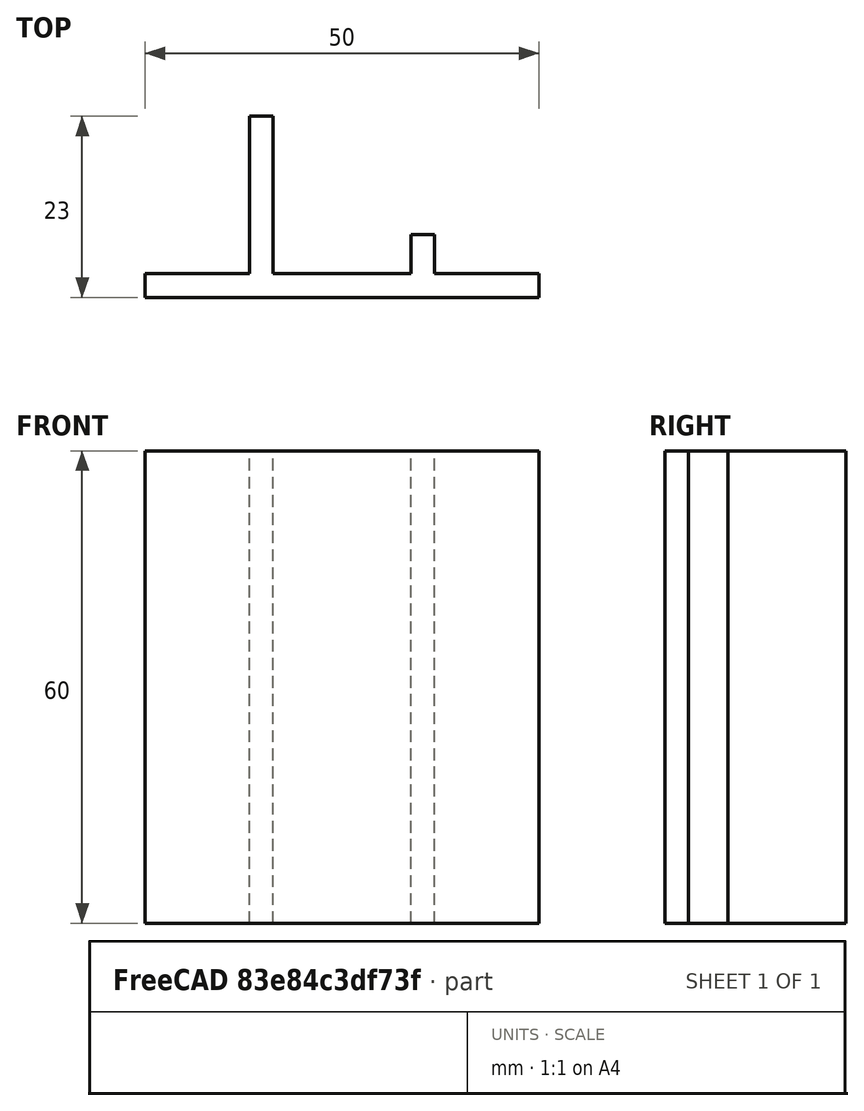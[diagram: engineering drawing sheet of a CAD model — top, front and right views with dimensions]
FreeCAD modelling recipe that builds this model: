
FCSTD DOCUMENT  (FreeCAD 0.20R29603 (Git))
Label: 3d_stand
License: All rights reserved
LicenseURL: http://en.wikipedia.org/wiki/All_rights_reserved
objects: Sketcher::SketchObject×1, PartDesign::Pad×1, PartDesign::Body×1
note: 4 computed .brp shape members not serialized (recipe doc carries the construction recipe); baked Part::Feature solids carry a one-line shape summary decoded from their .brp

FEATURE [Sketcher::SketchObject] Sketch
  FullyConstrained = true
  MapMode = 5
  Support = -> [XY_Plane]
  sketch-geometry (12):
    g0: LineSegment StartX=-24.88 StartY=-4.7 StartZ=0 EndX=25.12 EndY=-4.7 EndZ=0
    g1: LineSegment StartX=25.12 StartY=-4.7 StartZ=0 EndX=25.12 EndY=-1.7 EndZ=0
    g2: LineSegment StartX=25.12 StartY=-1.7 StartZ=0 EndX=11.87 EndY=-1.7 EndZ=0
    g3: LineSegment StartX=11.87 StartY=-1.7 StartZ=0 EndX=11.87 EndY=3.3 EndZ=0
    g4: LineSegment StartX=11.87 StartY=3.3 StartZ=0 EndX=8.87 EndY=3.3 EndZ=0
    g5: LineSegment StartX=8.87 StartY=3.3 StartZ=0 EndX=8.87 EndY=-1.7 EndZ=0
    g6: LineSegment StartX=8.87 StartY=-1.7 StartZ=0 EndX=-8.63 EndY=-1.7 EndZ=0
    g7: LineSegment StartX=-8.63 StartY=-1.7 StartZ=0 EndX=-8.63 EndY=18.3 EndZ=0
    g8: LineSegment StartX=-8.63 StartY=18.3 StartZ=0 EndX=-11.63 EndY=18.3 EndZ=0
    g9: LineSegment StartX=-11.63 StartY=18.3 StartZ=0 EndX=-11.63 EndY=-1.7 EndZ=0
    g10: LineSegment StartX=-11.63 StartY=-1.7 StartZ=0 EndX=-24.88 EndY=-1.7 EndZ=0
    g11: LineSegment StartX=-24.88 StartY=-1.7 StartZ=0 EndX=-24.88 EndY=-4.7 EndZ=0
  constraints (36):
    c: Horizontal(g0)
    c: Coincident(g0,g1)
    c: Vertical(g1)
    c: Coincident(g1,g2)
    c: Horizontal(g2)
    c: Coincident(g2,g3)
    c: Vertical(g3)
    c: Coincident(g3,g4)
    c: Horizontal(g4)
    c: Coincident(g4,g5)
    c: Vertical(g5)
    c: Coincident(g5,g6)
    c: Horizontal(g6)
    c: Coincident(g6,g7)
    c: Vertical(g7)
    c: Coincident(g7,g8)
    c: Horizontal(g8)
    c: Coincident(g8,g9)
    c: Vertical(g9)
    c: Coincident(g9,g10)
    c: Horizontal(g10)
    c: Coincident(g10,g11)
    c: Coincident(g11,g0)
    c: Vertical(g11)
    c: DistanceX(g4,g4) = 3
    c: DistanceX(g8,g8) = 3
    c: DistanceX(g6,g6) = 17.5
    c: DistanceY(g1,g1) = 3
    c: DistanceY(g11,g11) = 3
    c: DistanceY(g0,g6) = 3
    c: DistanceY(g9,g9) = 20
    c: DistanceY(g5,g5) = 5
    c: DistanceX(g0,g0) = 50
    c: DistanceX(g2,g2) = 13.25
    c: DistanceY(g6,g-1) = 1.7
    c: DistanceX(g6,g-1) = 8.63
FEATURE [PartDesign::Pad] Pad
  Direction = (0,0,1)
  Length = 60
  Length2 = 10
  Profile = -> Sketch
  ReferenceAxis = -> Sketch [N_Axis]
  Type = 0
FEATURE [PartDesign::Body] Body
  Group = -> [Sketch,Pad]
  Origin = -> Origin
  Tip = -> Pad
